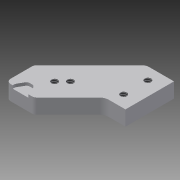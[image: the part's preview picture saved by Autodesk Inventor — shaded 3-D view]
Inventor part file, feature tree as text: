
AUTODESK INVENTOR PART (.ipt)
format: ipt  version: 2014 (Build 180170000, 170)  size: 124,928 bytes
history: native  units: in
note: dims shown in document units (in); Inventor stores cm internally (conversion verified against a paired STEP export)
features: other x3, plane x2
ambient origin geometry x8: Origin, YZ Plane, XZ Plane, XY Plane, X Axis, Y Axis, Z Axis, Center Point
bodies: Solid1 (feature_tree)
feature tree (5):
  other  "hph_A_001.ipt"
  other  "Solid1::hph_A_001.ipt"
  other  "TaggingFeature1"
  plane  "Work Plane1"
  plane  "Work Plane2"
